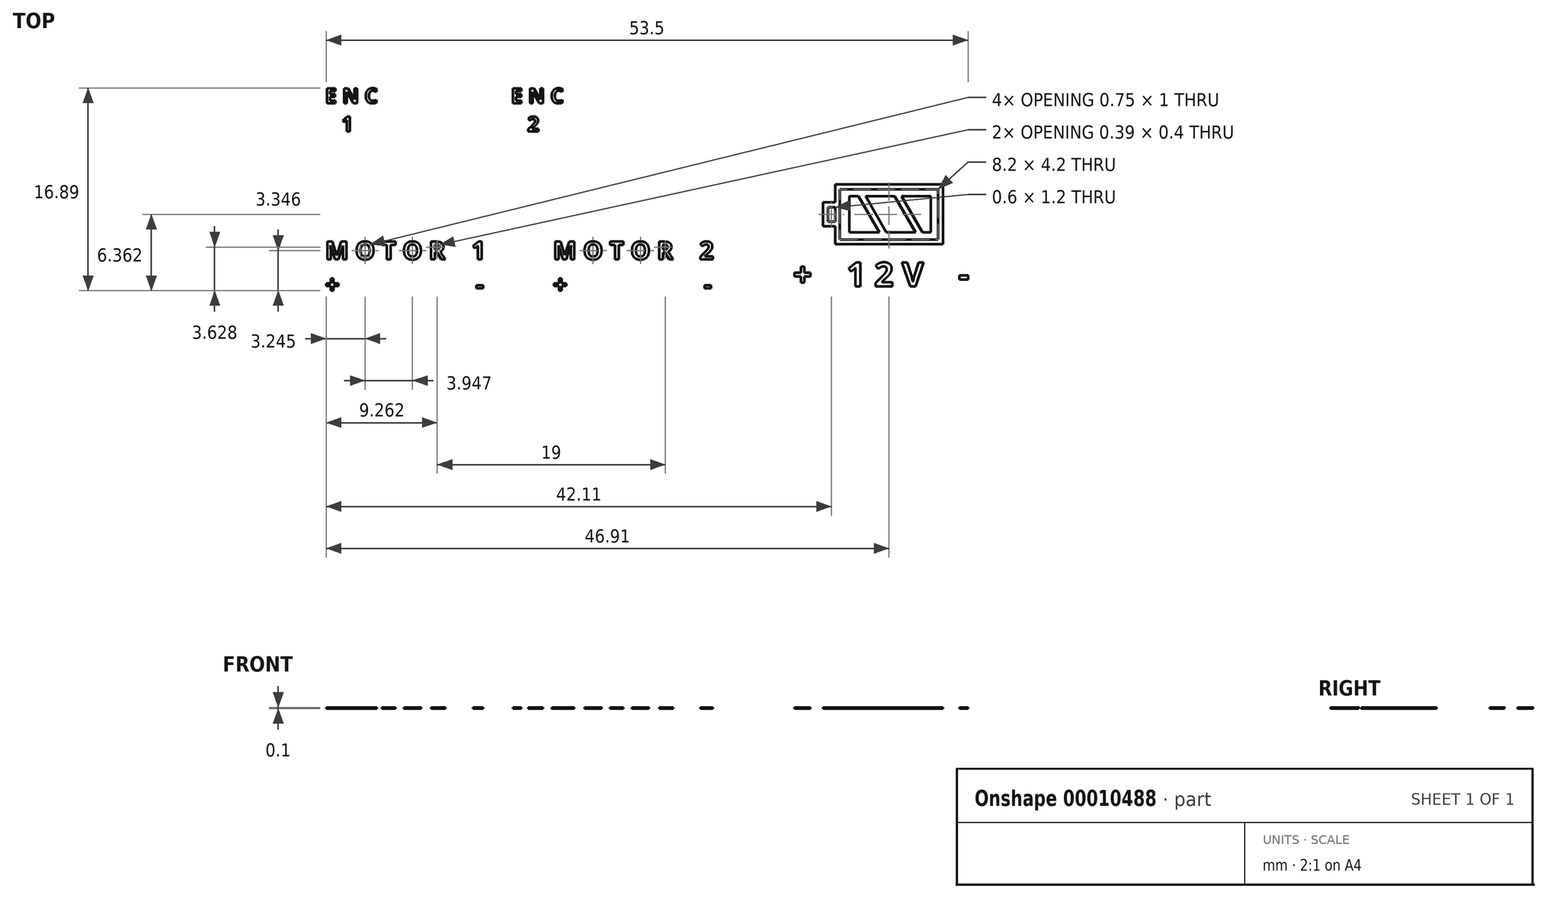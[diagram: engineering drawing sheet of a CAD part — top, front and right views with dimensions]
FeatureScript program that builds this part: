
annotation { "Feature Type Name" : "Feature", "Feature Type Description" : "" }
export const myFeature = defineFeature(function(context is Context, id is Id, definition is map)
    precondition{}
    {
        {
            var Q0;
            Q0=qCreatedBy(makeId("Top.planeOp"),FACE);
            var sketch = newSketch(context, id + "F0", { "sketchPlane" : qUnion([Q0])});
            skText(sketch, "E0", { "text": "E N C\n   1", "fontName": "OpenSans-Bold.ttf"});
            skText(sketch, "E1", { "text": "E N C\n   2", "fontName": "OpenSans-Bold.ttf"});
            skText(sketch, "E2", { "text": "M O T O R    1\n+                     -", "fontName": "OpenSans-Bold.ttf"});
            skText(sketch, "E3", { "text": "M O T O R    2\n+                     -", "fontName": "OpenSans-Bold.ttf"});
            skText(sketch, "E4", { "text": "+    1 2 V    -", "fontName": "OpenSans-Bold.ttf"});
            skLineSegment(sketch, "E5.bottom", {"start": v(42.9, -8.42) * mm, "end": v(51.1, -8.42) * mm});
            skLineSegment(sketch, "E5.top", {"start": v(42.9, -12.62) * mm, "end": v(51.1, -12.62) * mm});
            skLineSegment(sketch, "E5.left", {"start": v(42.9, -8.42) * mm, "end": v(42.9, -12.62) * mm});
            skLineSegment(sketch, "E5.right", {"start": v(51.1, -8.42) * mm, "end": v(51.1, -12.62) * mm});
            skLineSegment(sketch, "E6.rect.bottom", {"start": v(41.9, -9.92) * mm, "end": v(42.5, -9.92) * mm});
            skLineSegment(sketch, "E6.rect.top", {"start": v(41.9, -11.12) * mm, "end": v(42.5, -11.12) * mm});
            skLineSegment(sketch, "E6.rect.left", {"start": v(41.9, -9.92) * mm, "end": v(41.9, -11.12) * mm});
            skPoint(sketch, "E6.rect.middle", {"position": v(42.9, -10.52) * mm});
            skPoint(sketch, "E6.rect.right.start.orphan", {"position": v(43.9, -9.92) * mm});
            skPoint(sketch, "E7.orphan", {"position": v(43.9, -11.12) * mm});
            skLineSegment(sketch, "E8.0", {"start": v(41.5, -11.52) * mm, "end": v(42.5, -11.52) * mm});
            skLineSegment(sketch, "E8.1", {"start": v(41.5, -9.52) * mm, "end": v(41.5, -11.52) * mm});
            skLineSegment(sketch, "E8.2", {"start": v(41.5, -9.52) * mm, "end": v(42.5, -9.52) * mm});
            skLineSegment(sketch, "E9.0", {"start": v(42.5, -8.02) * mm, "end": v(42.5, -9.52) * mm});
            skLineSegment(sketch, "E9.1", {"start": v(42.5, -8.02) * mm, "end": v(51.5, -8.02) * mm});
            skLineSegment(sketch, "E9.2", {"start": v(51.5, -8.02) * mm, "end": v(51.5, -13.02) * mm});
            skLineSegment(sketch, "E9.3", {"start": v(42.5, -13.02) * mm, "end": v(51.5, -13.02) * mm});
            skLineSegment(sketch, "E10.trimOffspring", {"start": v(42.5, -9.92) * mm, "end": v(42.5, -11.12) * mm});
            skLineSegment(sketch, "E11.trimOffspring", {"start": v(42.5, -11.52) * mm, "end": v(42.5, -13.02) * mm});
            skLineSegment(sketch, "E12.rect.bottom", {"start": v(50.5, -9.02) * mm, "end": v(48.05, -9.02) * mm});
            skLineSegment(sketch, "E12.rect.top", {"start": v(50.5, -12.02) * mm, "end": v(49.78, -12.02) * mm});
            skLineSegment(sketch, "E12.rect.left", {"start": v(50.5, -9.02) * mm, "end": v(50.5, -12.02) * mm});
            skLineSegment(sketch, "E12.rect.right", {"start": v(43.7, -9.02) * mm, "end": v(43.7, -12.02) * mm});
            skPoint(sketch, "E12.rect.middle", {"position": v(47.1, -10.52) * mm});
            skLineSegment(sketch, "E13", {"start": v(45.05, -9.02) * mm, "end": v(46.78, -12.02) * mm});
            skLineSegment(sketch, "E14.0", {"start": v(44.47, -9.02) * mm, "end": v(46.2, -12.02) * mm});
            skLineSegment(sketch, "E15.1.0.0", {"start": v(47.47, -9.02) * mm, "end": v(49.2, -12.02) * mm});
            skLineSegment(sketch, "E15.1.0.1", {"start": v(48.05, -9.02) * mm, "end": v(49.78, -12.02) * mm});
            skLineSegment(sketch, "E15.direction1", {"start": v(46.95, -12.02) * mm, "end": v(49.95, -12.02) * mm, "construction": true});
            skLineSegment(sketch, "E16.trimOffspring", {"start": v(44.47, -9.02) * mm, "end": v(43.7, -9.02) * mm});
            skLineSegment(sketch, "E17.trimOffspring", {"start": v(47.47, -9.02) * mm, "end": v(45.05, -9.02) * mm});
            skLineSegment(sketch, "E18.trimOffspring", {"start": v(49.2, -12.02) * mm, "end": v(46.78, -12.02) * mm});
            skLineSegment(sketch, "E19.trimOffspring", {"start": v(46.2, -12.02) * mm, "end": v(43.7, -12.02) * mm});
            const initialGuessF0  = {"E0": [0, -0.00125, 1, 0, 0.00125], "E1": [0.0155, -0.00125, 1, 0, 0.00125], "E2": [0, -0.01428, 1, 0, 0.0015], "E3": [0.019, -0.01428, 1, 0, 0.0015], "E4": [0.039, -0.01652, 1, 0, 0.002]};
            skSetInitialGuess(sketch, initialGuessF0);
            skSolve(sketch);
        }
        {
            var Q0;
            Q0 = qSketchRegion(id + "F0", true);
            var Q1;
            Q1=makeQuery(id+"F0.imprint","IMPRINT",FACE,{"disambiguationData":[TD([[makeQuery(id+"F0.imprint","IMPRINT",EDGE,{"derivedFrom":sQuery(id+"F0.wireOp",EDGE,"E12.rect.right")}),1.0]])]});
            var Q2;
            Q2=makeQuery(id+"F0.imprint","IMPRINT",FACE,{"disambiguationData":[TD([[makeQuery(id+"F0.imprint","IMPRINT",EDGE,{"derivedFrom":sQuery(id+"F0.wireOp",EDGE,"E13")}),1.0]])]});
            var Q3;
            Q3=makeQuery(id+"F0.imprint","IMPRINT",FACE,{"disambiguationData":[TD([[makeQuery(id+"F0.imprint","IMPRINT",EDGE,{"derivedFrom":sQuery(id+"F0.wireOp",EDGE,"E12.rect.bottom")}),1.0]])]});
            extrude(context, id + "F1", {"entities" : qUnion([Q0, Q1, Q2, Q3]), "depth" : .1 * mm});
        }
    });
